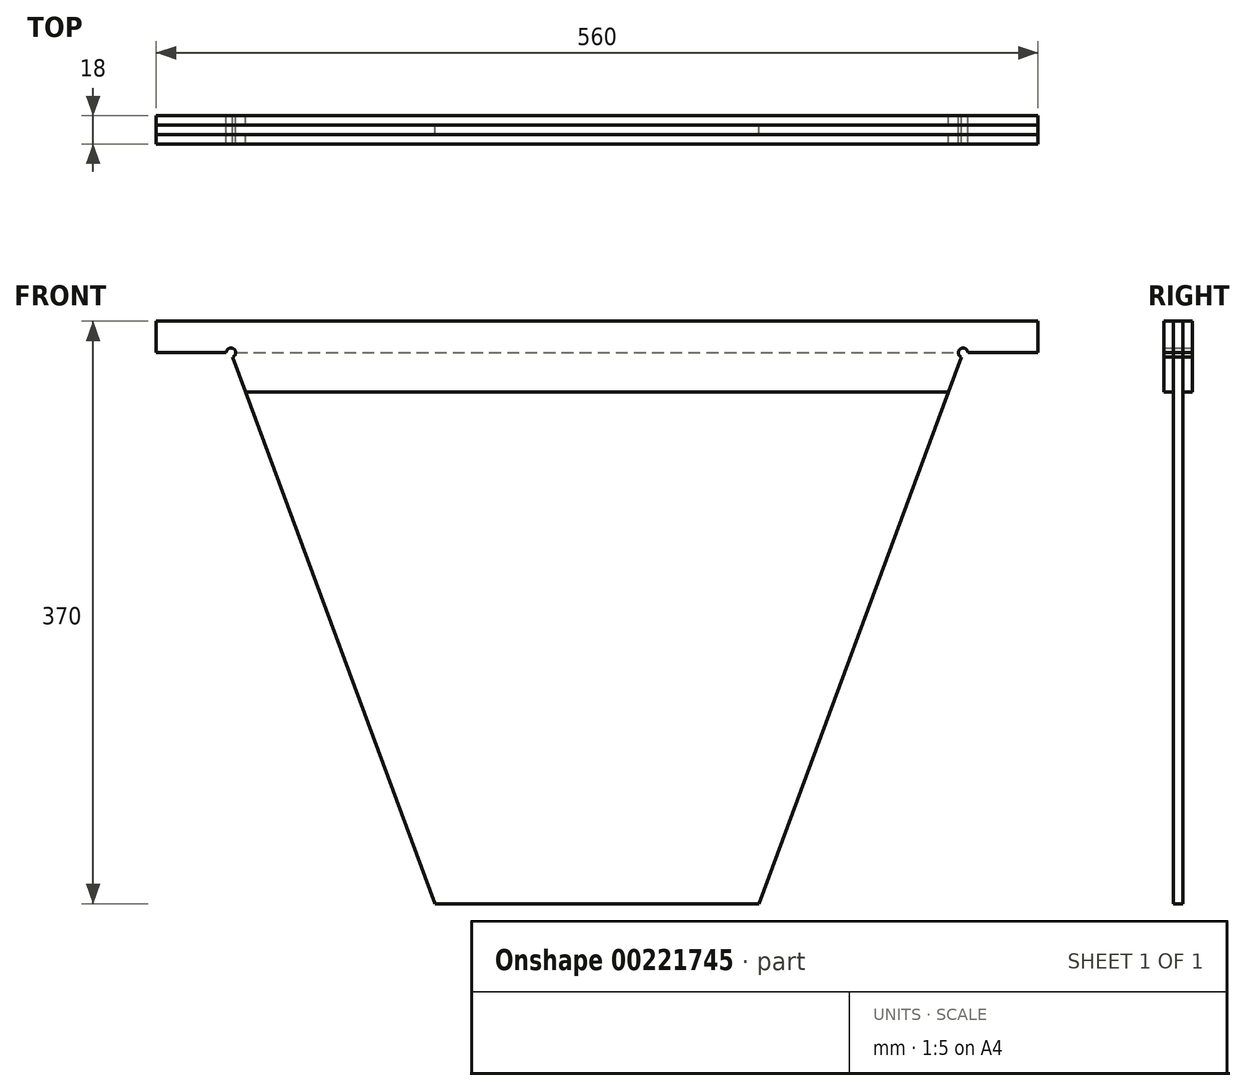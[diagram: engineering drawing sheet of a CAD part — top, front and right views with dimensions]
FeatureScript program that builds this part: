
annotation { "Feature Type Name" : "Feature", "Feature Type Description" : "" }
export const myFeature = defineFeature(function(context is Context, id is Id, definition is map)
    precondition{}
    {
        {
            var Q0;
            Q0=qCreatedBy(makeId("Front.planeOp"),FACE);
            var sketch = newSketch(context, id + "F0", { "sketchPlane" : qUnion([Q0])});
            skLineSegment(sketch, "E0", {"start": v(0, 0) * mm, "end": v(0, -350) * mm, "construction": true});
            skLineSegment(sketch, "E1", {"start": v(0, -350) * mm, "end": v(-103, -350) * mm});
            skLineSegment(sketch, "E2", {"start": v(-103, -350) * mm, "end": v(-232.5, 0) * mm});
            skLineSegment(sketch, "E3", {"start": v(232.5, 0) * mm, "end": v(-232.5, 0) * mm});
            skLineSegment(sketch, "E4.MirrorCS", {"start": v(103, -350) * mm, "end": v(232.5, 0) * mm});
            skLineSegment(sketch, "E5.MirrorCS", {"start": v(0, -350) * mm, "end": v(103, -350) * mm});
            skSolve(sketch);
        }
        {
            var Q0;
            Q0 = qSketchRegion(id + "F0", true);
            extrude(context, id + "F1", {"entities" : qUnion([Q0]), "endBound" : BoundingType.SYMMETRIC, "depth" : 6 * mm});
        }
        {
            var Q0;
            Q0=makeQuery(id+"F1.opExtrude","CAP_FACE",FACE,{"disambiguationData":[OSD([sQuery(id+"F0.wireOp",EDGE,"E1"),sQuery(id+"F0.wireOp",EDGE,"E2"),sQuery(id+"F0.wireOp",EDGE,"E3"),sQuery(id+"F0.wireOp",EDGE,"E4.MirrorCS"),sQuery(id+"F0.wireOp",EDGE,"E5.MirrorCS")])],"isStart":false});
            var sketch = newSketch(context, id + "F2", { "sketchPlane" : qUnion([Q0])});
            skLineSegment(sketch, "E6.bottom", {"start": v(-280, -25) * mm, "end": v(280, -25) * mm});
            skLineSegment(sketch, "E6.top", {"start": v(-280, 20) * mm, "end": v(280, 20) * mm});
            skLineSegment(sketch, "E6.left", {"start": v(-280, -25) * mm, "end": v(-280, 20) * mm});
            skLineSegment(sketch, "E6.right", {"start": v(280, -25) * mm, "end": v(280, 20) * mm});
            skPoint(sketch, "E6.middle", {"position": v(0, 0) * mm});
            skLineSegment(sketch, "E7", {"start": v(0, 0) * mm, "end": v(0, -84.28) * mm, "construction": true});
            skSolve(sketch);
        }
        {
            var Q0;
            Q0=makeQuery(id+"F2.imprint","IMPRINT",FACE,{"disambiguationData":[TD([[makeQuery(id+"F2.imprint","IMPRINT",EDGE,{"derivedFrom":sQuery(id+"F2.wireOp",EDGE,"E6.top")}),-1.0]])]});
            var Q1;
            {var subQ5=makeQuery(id+"F1.opExtrude","CAP_EDGE",EDGE,{"disambiguationData":[OSD([sQuery(id+"F0.wireOp",EDGE,"E3")])],"isStart":false});Q1=makeQuery(id+"F2.imprint","IMPRINT",FACE,{"disambiguationData":[TD([[makeQuery(id+"F2.imprint","IMPRINT",EDGE,{"derivedFrom":subQ5}),1.0]])]});}
            extrude(context, id + "F3", {"entities" : qUnion([Q0, Q1]), "depth" : 6 * mm});
        }
        {
            var Q0;
            Q0=makeQuery(id+"F1.opExtrude","CAP_FACE",FACE,{"disambiguationData":[OSD([sQuery(id+"F0.wireOp",EDGE,"E1"),sQuery(id+"F0.wireOp",EDGE,"E2"),sQuery(id+"F0.wireOp",EDGE,"E3"),sQuery(id+"F0.wireOp",EDGE,"E4.MirrorCS"),sQuery(id+"F0.wireOp",EDGE,"E5.MirrorCS")])],"isStart":true});
            var sketch = newSketch(context, id + "F4", { "sketchPlane" : qUnion([Q0])});
            skLineSegment(sketch, "E8.0.0", {"start": v(-280, -25) * mm, "end": v(280, -25) * mm});
            skLineSegment(sketch, "E8.0.1", {"start": v(280, -25) * mm, "end": v(280, 20) * mm});
            skLineSegment(sketch, "E8.0.2", {"start": v(280, 20) * mm, "end": v(-280, 20) * mm});
            skLineSegment(sketch, "E8.0.3", {"start": v(-280, 20) * mm, "end": v(-280, -25) * mm});
            skSolve(sketch);
        }
        {
            var Q0;
            Q0 = qSketchRegion(id + "F4", true);
            extrude(context, id + "F5", {"entities" : qUnion([Q0]), "depth" : 6 * mm});
        }
        {
            var Q0;
            Q0=makeQuery(id+"F3.opExtrude","CAP_FACE",FACE,{"disambiguationData":[OSD([sQuery(id+"F2.wireOp",EDGE,"E6.bottom"),sQuery(id+"F2.wireOp",EDGE,"E6.top"),sQuery(id+"F2.wireOp",EDGE,"E6.left"),sQuery(id+"F2.wireOp",EDGE,"E6.right")])],"isStart":true});
            var sketch = newSketch(context, id + "F6", { "sketchPlane" : qUnion([Q0])});
            skLineSegment(sketch, "E9.0.0", {"start": v(-280, -25) * mm, "end": v(280, -25) * mm});
            skLineSegment(sketch, "E9.0.1", {"start": v(280, -25) * mm, "end": v(280, 20) * mm});
            skLineSegment(sketch, "E9.0.2", {"start": v(280, 20) * mm, "end": v(-280, 20) * mm});
            skLineSegment(sketch, "E9.0.3", {"start": v(-280, 20) * mm, "end": v(-280, -25) * mm});
            skLineSegment(sketch, "E10.0.0", {"start": v(-103, -350) * mm, "end": v(103, -350) * mm});
            skLineSegment(sketch, "E10.0.1", {"start": v(103, -350) * mm, "end": v(232.5, 0) * mm});
            skLineSegment(sketch, "E10.0.2", {"start": v(232.5, 0) * mm, "end": v(-232.5, 0) * mm});
            skLineSegment(sketch, "E10.0.3", {"start": v(-232.5, 0) * mm, "end": v(-103, -350) * mm});
            skSolve(sketch);
        }
        {
            var Q0;
            {var subQ0=sQuery(id+"F6.wireOp",EDGE,"E9.0.1");Q0=makeQuery(id+"F6.imprint","IMPRINT",FACE,{"disambiguationData":[TD([[makeQuery(id+"F6.imprint","IMPRINT",EDGE,{"derivedFrom":subQ0}),1.0]])]});}
            extrude(context, id + "F7", {"entities" : qUnion([Q0]), "depth" : 6 * mm});
        }
        {
            var Q0;
            Q0=makeQuery(id+"F5.opExtrude","CAP_FACE",FACE,{"disambiguationData":[OSD([sQuery(id+"F4.wireOp",EDGE,"E8.0.0"),sQuery(id+"F4.wireOp",EDGE,"E8.0.1"),sQuery(id+"F4.wireOp",EDGE,"E8.0.2"),sQuery(id+"F4.wireOp",EDGE,"E8.0.3")])],"isStart":false});
            var sketch = newSketch(context, id + "F8", { "sketchPlane" : qUnion([Q0])});
            skLineSegment(sketch, "E11", {"start": v(-280, 0) * mm, "end": v(-218.07, 0) * mm});
            skLineSegment(sketch, "E12", {"start": v(-280, 0) * mm, "end": v(-280, -25) * mm});
            skLineSegment(sketch, "E13", {"start": v(-280, -25) * mm, "end": v(-223.28, -25) * mm});
            skLineSegment(sketch, "E14.0", {"start": v(-232.5, 0) * mm, "end": v(-103, -350) * mm});
            skLineSegment(sketch, "E15.0", {"start": v(0, 0) * mm, "end": v(0, -84.28) * mm, "construction": true});
            skLineSegment(sketch, "E16.MirrorCS", {"start": v(280, 0) * mm, "end": v(218.07, 0) * mm});
            skLineSegment(sketch, "E17.MirrorCS", {"start": v(280, 0) * mm, "end": v(280, -25) * mm});
            skLineSegment(sketch, "E18.MirrorCS", {"start": v(280, -25) * mm, "end": v(223.28, -25) * mm});
            skLineSegment(sketch, "E19.MirrorCS", {"start": v(232.5, 0) * mm, "end": v(103, -350) * mm});
            skCircle(sketch, "E20", {"center": v(-232.5, 0) * mm, "radius": 3 * mm});
            skCircle(sketch, "E21.MirrorC", {"center": v(232.5, 0) * mm, "radius": 3 * mm});
            skSolve(sketch);
        }
        {
            var Q0;
            {var subQ6=sQuery(id+"F8.wireOp",EDGE,"E12");Q0=makeQuery(id+"F8.imprint","IMPRINT",FACE,{"disambiguationData":[TD([[makeQuery(id+"F8.imprint","IMPRINT",EDGE,{"derivedFrom":subQ6}),1.0]])]});}
            var Q1;
            {var subQ6=sQuery(id+"F8.wireOp",EDGE,"E17.MirrorCS");Q1=makeQuery(id+"F8.imprint","IMPRINT",FACE,{"disambiguationData":[TD([[makeQuery(id+"F8.imprint","IMPRINT",EDGE,{"derivedFrom":subQ6}),1.0]])]});}
            var Q2;
            {var subQ0=sQuery(id+"F8.wireOp",EDGE,"E14.0");var subQ1=sQuery(id+"F8.wireOp",EDGE,"E11");var subQ2=makeQuery(id+"F8.imprint","INTERSECT",VERTEX,{"derivedFrom":[subQ1,subQ0]});Q2=makeQuery(id+"F8.imprint","IMPRINT",FACE,{"disambiguationData":[TD([[makeQuery(id+"F8.imprint","IMPRINT",EDGE,{"disambiguationData":[TD([[subQ2,1.0]])],"derivedFrom":subQ1}),-1.0]])]});}
            var Q3;
            {var subQ0=sQuery(id+"F8.wireOp",EDGE,"E14.0");var subQ1=sQuery(id+"F8.wireOp",EDGE,"E11");var subQ2=makeQuery(id+"F8.imprint","INTERSECT",VERTEX,{"derivedFrom":[subQ1,subQ0]});Q3=makeQuery(id+"F8.imprint","IMPRINT",FACE,{"disambiguationData":[TD([[makeQuery(id+"F8.imprint","IMPRINT",EDGE,{"disambiguationData":[TD([[subQ2,-1.0]])],"derivedFrom":subQ1}),-1.0]])]});}
            var Q4;
            {var subQ0=sQuery(id+"F8.wireOp",EDGE,"E11");var subQ1=makeQuery(id+"F8.imprint","INTERSECT",VERTEX,{"derivedFrom":[subQ0,sQuery(id+"F8.wireOp",EDGE,"E14.0")]});Q4=makeQuery(id+"F8.imprint","IMPRINT",FACE,{"disambiguationData":[TD([[makeQuery(id+"F8.imprint","IMPRINT",EDGE,{"disambiguationData":[TD([[subQ1,1.0]])],"derivedFrom":subQ0}),1.0]])]});}
            var Q5;
            {var subQ0=sQuery(id+"F8.wireOp",EDGE,"E19.MirrorCS");var subQ1=sQuery(id+"F8.wireOp",EDGE,"E16.MirrorCS");var subQ2=makeQuery(id+"F8.imprint","INTERSECT",VERTEX,{"derivedFrom":[subQ1,subQ0]});Q5=makeQuery(id+"F8.imprint","IMPRINT",FACE,{"disambiguationData":[TD([[makeQuery(id+"F8.imprint","IMPRINT",EDGE,{"disambiguationData":[TD([[subQ2,1.0]])],"derivedFrom":subQ1}),1.0]])]});}
            var Q6;
            {var subQ0=sQuery(id+"F8.wireOp",EDGE,"E16.MirrorCS");var subQ1=makeQuery(id+"F8.imprint","INTERSECT",VERTEX,{"derivedFrom":[subQ0,sQuery(id+"F8.wireOp",EDGE,"E19.MirrorCS")]});Q6=makeQuery(id+"F8.imprint","IMPRINT",FACE,{"disambiguationData":[TD([[makeQuery(id+"F8.imprint","IMPRINT",EDGE,{"disambiguationData":[TD([[subQ1,1.0]])],"derivedFrom":subQ0}),-1.0]])]});}
            var Q7;
            {var subQ0=sQuery(id+"F8.wireOp",EDGE,"E19.MirrorCS");var subQ1=sQuery(id+"F8.wireOp",EDGE,"E16.MirrorCS");var subQ2=makeQuery(id+"F8.imprint","INTERSECT",VERTEX,{"derivedFrom":[subQ1,subQ0]});Q7=makeQuery(id+"F8.imprint","IMPRINT",FACE,{"disambiguationData":[TD([[makeQuery(id+"F8.imprint","IMPRINT",EDGE,{"disambiguationData":[TD([[subQ2,-1.0]])],"derivedFrom":subQ1}),1.0]])]});}
            extrude(context, id + "F9", {"entities" : qUnion([Q0, Q1, Q2, Q3, Q4, Q5, Q6, Q7]), "operationType" : NewBodyOperationType.REMOVE, "endBound" : BoundingType.THROUGH_ALL, "oppositeDirection" : true, "depth" : 25 * mm});
        }
    });
